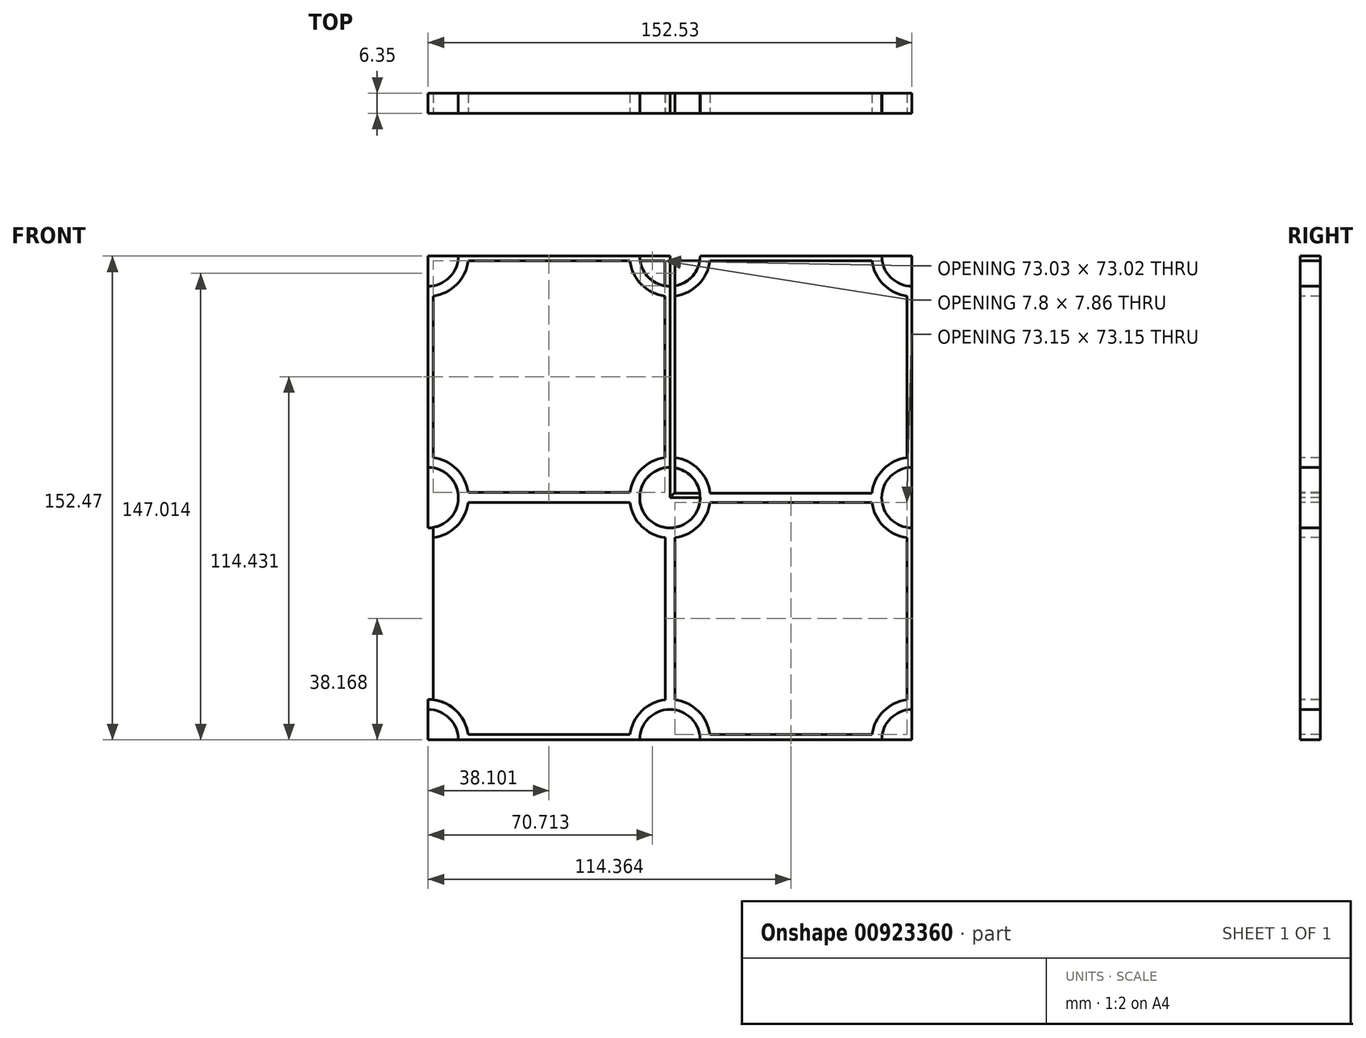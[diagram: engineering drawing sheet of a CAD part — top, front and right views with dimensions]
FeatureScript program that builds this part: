
annotation { "Feature Type Name" : "Feature", "Feature Type Description" : "" }
export const myFeature = defineFeature(function(context is Context, id is Id, definition is map)
    precondition{}
    {
        {
            var Q0;
            Q0=qCreatedBy(makeId("Front.planeOp"),FACE);
            var sketch = newSketch(context, id + "F0", { "sketchPlane" : qUnion([Q0])});
            skLineSegment(sketch, "E0.bottom", {"start": v(-162.8, 108.2) * mm, "end": v(-89.78, 108.2) * mm});
            skLineSegment(sketch, "E0.top", {"start": v(-162.8, 35.18) * mm, "end": v(-89.78, 35.18) * mm});
            skLineSegment(sketch, "E0.left", {"start": v(-162.8, 108.2) * mm, "end": v(-162.8, 35.18) * mm});
            skLineSegment(sketch, "E0.right", {"start": v(-89.78, 108.2) * mm, "end": v(-89.78, 35.18) * mm});
            skLineSegment(sketch, "E1", {"start": v(-162.8, 108.2) * mm, "end": v(-164.39, 108.2) * mm});
            skLineSegment(sketch, "E2", {"start": v(-164.39, 121.61) * mm, "end": v(-164.39, -64.06) * mm});
            skLineSegment(sketch, "E3", {"start": v(-86.6, 108.2) * mm, "end": v(-86.6, 35.26) * mm});
            skLineSegment(sketch, "E4.bottom", {"start": v(-86.6, 108.2) * mm, "end": v(-13.45, 108.2) * mm});
            skLineSegment(sketch, "E4.top", {"start": v(-86.6, 35) * mm, "end": v(-13.45, 35) * mm});
            skLineSegment(sketch, "E4.left", {"start": v(-86.6, 108.2) * mm, "end": v(-86.6, 35) * mm});
            skLineSegment(sketch, "E4.right", {"start": v(-13.45, 108.2) * mm, "end": v(-13.45, 35) * mm});
            skLineSegment(sketch, "E5.bottom", {"start": v(-162.8, 32) * mm, "end": v(-89.65, 32) * mm});
            skLineSegment(sketch, "E5.top", {"start": v(-162.8, -41.15) * mm, "end": v(-89.65, -41.15) * mm});
            skLineSegment(sketch, "E5.left", {"start": v(-162.8, 32) * mm, "end": v(-162.8, -41.15) * mm});
            skLineSegment(sketch, "E5.right", {"start": v(-89.65, 32) * mm, "end": v(-89.65, -41.15) * mm});
            skLineSegment(sketch, "E6.bottom", {"start": v(-86.6, 32) * mm, "end": v(-13.45, 32) * mm});
            skLineSegment(sketch, "E6.top", {"start": v(-86.6, -41.15) * mm, "end": v(-13.45, -41.15) * mm});
            skLineSegment(sketch, "E6.left", {"start": v(-86.6, 32) * mm, "end": v(-86.6, -41.15) * mm});
            skLineSegment(sketch, "E6.right", {"start": v(-13.45, 32) * mm, "end": v(-13.45, -41.15) * mm});
            skLineSegment(sketch, "E7", {"start": v(-86.6, 35.26) * mm, "end": v(-89.65, 32) * mm});
            skLineSegment(sketch, "E8", {"start": v(-89.78, 35.18) * mm, "end": v(-86.6, 32) * mm});
            skCircle(sketch, "E9", {"center": v(-88.18, 33.58) * mm, "radius": 9.53 * mm});
            skCircle(sketch, "E10", {"center": v(-88.18, 33.58) * mm, "radius": 12.7 * mm});
            skLineSegment(sketch, "E11.0", {"start": v(-200.1, 109.73) * mm, "end": v(15.54, 109.73) * mm});
            skPoint(sketch, "E12.orphan", {"position": v(-164.39, 0) * mm});
            skLineSegment(sketch, "E13.0", {"start": v(-212.16, -42.74) * mm, "end": v(20.66, -42.74) * mm});
            skLineSegment(sketch, "E14.0", {"start": v(-11.86, 123.44) * mm, "end": v(-11.86, -68.08) * mm});
            skLineSegment(sketch, "E15", {"start": v(-11.86, 33.58) * mm, "end": v(-190.66, 33.58) * mm});
            skLineSegment(sketch, "E16", {"start": v(-88.18, 109.73) * mm, "end": v(-88.18, -48) * mm});
            skLineSegment(sketch, "E17", {"start": v(-88.18, -48) * mm, "end": v(-87.03, -48) * mm});
            skCircle(sketch, "E18", {"center": v(-164.39, 109.73) * mm, "radius": 12.7 * mm});
            skCircle(sketch, "E19", {"center": v(-88.18, 109.73) * mm, "radius": 12.7 * mm});
            skCircle(sketch, "E20", {"center": v(-11.86, 109.73) * mm, "radius": 12.7 * mm});
            skCircle(sketch, "E21", {"center": v(-11.86, 33.58) * mm, "radius": 12.7 * mm});
            skCircle(sketch, "E22", {"center": v(-88.18, -42.74) * mm, "radius": 12.7 * mm});
            skCircle(sketch, "E23", {"center": v(-164.39, 33.58) * mm, "radius": 12.7 * mm});
            skCircle(sketch, "E24", {"center": v(-164.39, 33.58) * mm, "radius": 9.53 * mm});
            skCircle(sketch, "E25", {"center": v(-88.18, -42.74) * mm, "radius": 9.53 * mm});
            skCircle(sketch, "E26", {"center": v(-164.39, -42.74) * mm, "radius": 9.53 * mm});
            skCircle(sketch, "E27", {"center": v(-11.86, -42.74) * mm, "radius": 9.53 * mm});
            skCircle(sketch, "E28", {"center": v(-11.86, 33.58) * mm, "radius": 9.53 * mm});
            skCircle(sketch, "E29", {"center": v(-11.86, 109.73) * mm, "radius": 9.53 * mm});
            skCircle(sketch, "E30", {"center": v(-88.18, 109.73) * mm, "radius": 9.53 * mm});
            skCircle(sketch, "E31", {"center": v(-164.39, 109.73) * mm, "radius": 9.53 * mm});
            skCircle(sketch, "E32", {"center": v(-164.39, -42.74) * mm, "radius": 12.7 * mm});
            skCircle(sketch, "E33", {"center": v(-11.86, -42.74) * mm, "radius": 12.7 * mm});
            skSolve(sketch);
        }
        {
            var Q0;
            Q0=makeQuery(id+"F0.imprint","IMPRINT",FACE,{"disambiguationData":[TD([[makeQuery(id+"F0.imprint","IMPRINT",EDGE,{"derivedFrom":sQuery(id+"F0.wireOp",EDGE,"E0.bottom")}),-1.0]])]});
            extrude(context, id + "F1", {"entities" : qUnion([Q0]), "oppositeDirection" : true, "depth" : 6.35 * mm, "offsetDistance" : 30.48 * mm});
        }
        {
            var Q0;
            Q0=makeQuery(id+"F1.opExtrude","SWEPT_BODY",BODY,{"disambiguationData":[OSD([sQuery(id+"F0.wireOp",EDGE,"E0.bottom"),sQuery(id+"F0.wireOp",EDGE,"E0.left"),sQuery(id+"F0.wireOp",EDGE,"E31")])]});
            deleteBodies(context, id + "F2", {"entities" : qUnion([Q0])});
        }
        {
            var Q0;
            Q0=makeQuery(id+"F1.opExtrude","SWEPT_BODY",BODY,{"disambiguationData":[OSD([sQuery(id+"F0.wireOp",EDGE,"E0.bottom"),sQuery(id+"F0.wireOp",EDGE,"E0.right"),sQuery(id+"F0.wireOp",EDGE,"E30")])]});
            deleteBodies(context, id + "F3", {"entities" : qUnion([Q0])});
        }
        {
            var Q0;
            {var subQ7=sQuery(id+"F0.wireOp",EDGE,"E18");var subQ13=sQuery(id+"F0.wireOp",EDGE,"E0.bottom");var subQ14=makeQuery(id+"F0.imprint","INTERSECT",VERTEX,{"derivedFrom":[subQ13,subQ7]});Q0=makeQuery(id+"F0.imprint","IMPRINT",FACE,{"disambiguationData":[TD([[makeQuery(id+"F0.imprint","IMPRINT",EDGE,{"disambiguationData":[TD([[subQ14,-1.0]])],"derivedFrom":subQ13}),-1.0]])]});}
            var Q1;
            {var subQ9=sQuery(id+"F0.wireOp",EDGE,"E19");var subQ13=sQuery(id+"F0.wireOp",EDGE,"E4.bottom");var subQ14=makeQuery(id+"F0.imprint","INTERSECT",VERTEX,{"derivedFrom":[subQ13,subQ9]});Q1=makeQuery(id+"F0.imprint","IMPRINT",FACE,{"disambiguationData":[TD([[makeQuery(id+"F0.imprint","IMPRINT",EDGE,{"disambiguationData":[TD([[subQ14,-1.0]])],"derivedFrom":subQ13}),-1.0]])]});}
            var Q2;
            {var subQ10=sQuery(id+"F0.wireOp",EDGE,"E10");var subQ13=sQuery(id+"F0.wireOp",EDGE,"E6.bottom");var subQ14=makeQuery(id+"F0.imprint","INTERSECT",VERTEX,{"derivedFrom":[subQ13,subQ10]});Q2=makeQuery(id+"F0.imprint","IMPRINT",FACE,{"disambiguationData":[TD([[makeQuery(id+"F0.imprint","IMPRINT",EDGE,{"disambiguationData":[TD([[subQ14,-1.0]])],"derivedFrom":subQ13}),-1.0]])]});}
            var Q3;
            {var subQ10=sQuery(id+"F0.wireOp",EDGE,"E23");var subQ13=sQuery(id+"F0.wireOp",EDGE,"E5.bottom");var subQ14=makeQuery(id+"F0.imprint","INTERSECT",VERTEX,{"derivedFrom":[subQ13,subQ10]});Q3=makeQuery(id+"F0.imprint","IMPRINT",FACE,{"disambiguationData":[TD([[makeQuery(id+"F0.imprint","IMPRINT",EDGE,{"disambiguationData":[TD([[subQ14,-1.0]])],"derivedFrom":subQ13}),-1.0]])]});}
            extrude(context, id + "F4", {"entities" : qUnion([Q0, Q1, Q2, Q3]), "oppositeDirection" : true, "depth" : 6.35 * mm, "offsetDistance" : 30.48 * mm});
        }
        {
            var Q0;
            {var subQ0=sQuery(id+"F0.wireOp",EDGE,"E0.left");var subQ1=sQuery(id+"F0.wireOp",EDGE,"E0.top");var subQ2=makeQuery(id+"F0.imprint","INTERSECT",VERTEX,{"derivedFrom":[subQ1,subQ0]});Q0=makeQuery(id+"F0.imprint","IMPRINT",FACE,{"disambiguationData":[TD([[makeQuery(id+"F0.imprint","IMPRINT",EDGE,{"disambiguationData":[TD([[subQ2,-1.0]])],"derivedFrom":subQ1}),1.0]])]});}
            var Q1;
            {var subQ0=sQuery(id+"F0.wireOp",EDGE,"E5.left");var subQ1=sQuery(id+"F0.wireOp",EDGE,"E5.bottom");var subQ2=makeQuery(id+"F0.imprint","INTERSECT",VERTEX,{"derivedFrom":[subQ1,subQ0]});Q1=makeQuery(id+"F0.imprint","IMPRINT",FACE,{"disambiguationData":[TD([[makeQuery(id+"F0.imprint","IMPRINT",EDGE,{"disambiguationData":[TD([[subQ2,-1.0]])],"derivedFrom":subQ1}),-1.0]])]});}
            var Q2;
            {var subQ0=sQuery(id+"F0.wireOp",EDGE,"E4.left");var subQ1=sQuery(id+"F0.wireOp",EDGE,"E4.top");var subQ2=makeQuery(id+"F0.imprint","INTERSECT",VERTEX,{"derivedFrom":[subQ1,subQ0]});Q2=makeQuery(id+"F0.imprint","IMPRINT",FACE,{"disambiguationData":[TD([[makeQuery(id+"F0.imprint","IMPRINT",EDGE,{"disambiguationData":[TD([[subQ2,-1.0]])],"derivedFrom":subQ1}),1.0]])]});}
            var Q3;
            {var subQ1=sQuery(id+"F0.wireOp",EDGE,"E0.top");var subQ3=sQuery(id+"F0.wireOp",EDGE,"E9");var subQ4=makeQuery(id+"F0.imprint","INTERSECT",VERTEX,{"derivedFrom":[subQ1,subQ3]});Q3=makeQuery(id+"F0.imprint","IMPRINT",FACE,{"disambiguationData":[TD([[makeQuery(id+"F0.imprint","IMPRINT",EDGE,{"disambiguationData":[TD([[subQ4,1.0]])],"derivedFrom":subQ3}),1.0]])]});}
            var Q4;
            {var subQ1=sQuery(id+"F0.wireOp",EDGE,"E5.bottom");var subQ3=sQuery(id+"F0.wireOp",EDGE,"E9");var subQ4=makeQuery(id+"F0.imprint","INTERSECT",VERTEX,{"derivedFrom":[subQ1,subQ3]});Q4=makeQuery(id+"F0.imprint","IMPRINT",FACE,{"disambiguationData":[TD([[makeQuery(id+"F0.imprint","IMPRINT",EDGE,{"disambiguationData":[TD([[subQ4,-1.0]])],"derivedFrom":subQ3}),1.0]])]});}
            var Q5;
            {var subQ1=sQuery(id+"F0.wireOp",EDGE,"E6.bottom");var subQ3=sQuery(id+"F0.wireOp",EDGE,"E9");var subQ4=makeQuery(id+"F0.imprint","INTERSECT",VERTEX,{"derivedFrom":[subQ1,subQ3]});Q5=makeQuery(id+"F0.imprint","IMPRINT",FACE,{"disambiguationData":[TD([[makeQuery(id+"F0.imprint","IMPRINT",EDGE,{"disambiguationData":[TD([[subQ4,1.0]])],"derivedFrom":subQ3}),1.0]])]});}
            var Q6;
            {var subQ0=sQuery(id+"F0.wireOp",EDGE,"E7");var subQ1=sQuery(id+"F0.wireOp",EDGE,"E4.left");var subQ2=makeQuery(id+"F0.imprint","INTERSECT",VERTEX,{"derivedFrom":[subQ1,subQ0]});Q6=makeQuery(id+"F0.imprint","IMPRINT",FACE,{"disambiguationData":[TD([[makeQuery(id+"F0.imprint","IMPRINT",EDGE,{"disambiguationData":[TD([[subQ2,1.0]])],"derivedFrom":subQ1}),-1.0]])]});}
            var Q7;
            {var subQ1=sQuery(id+"F0.wireOp",EDGE,"E4.left");var subQ6=sQuery(id+"F0.wireOp",EDGE,"E4.top");var subQ9=makeQuery(id+"F0.imprint","INTERSECT",VERTEX,{"derivedFrom":[subQ6,subQ1]});Q7=makeQuery(id+"F0.imprint","IMPRINT",FACE,{"disambiguationData":[TD([[makeQuery(id+"F0.imprint","IMPRINT",EDGE,{"disambiguationData":[TD([[subQ9,-1.0]])],"derivedFrom":subQ6}),-1.0]])]});}
            var Q8;
            {var subQ1=sQuery(id+"F0.wireOp",EDGE,"E6.bottom");var subQ3=sQuery(id+"F0.wireOp",EDGE,"E9");var subQ4=makeQuery(id+"F0.imprint","INTERSECT",VERTEX,{"derivedFrom":[subQ1,subQ3]});Q8=makeQuery(id+"F0.imprint","IMPRINT",FACE,{"disambiguationData":[TD([[makeQuery(id+"F0.imprint","IMPRINT",EDGE,{"disambiguationData":[TD([[subQ4,-1.0]])],"derivedFrom":subQ3}),1.0]])]});}
            var Q9;
            {var subQ1=sQuery(id+"F0.wireOp",EDGE,"E6.left");var subQ3=sQuery(id+"F0.wireOp",EDGE,"E9");var subQ4=makeQuery(id+"F0.imprint","INTERSECT",VERTEX,{"derivedFrom":[subQ1,subQ3]});Q9=makeQuery(id+"F0.imprint","IMPRINT",FACE,{"disambiguationData":[TD([[makeQuery(id+"F0.imprint","IMPRINT",EDGE,{"disambiguationData":[TD([[subQ4,1.0]])],"derivedFrom":subQ3}),1.0]])]});}
            var Q10;
            {var subQ1=sQuery(id+"F0.wireOp",EDGE,"E5.right");var subQ3=sQuery(id+"F0.wireOp",EDGE,"E9");var subQ4=makeQuery(id+"F0.imprint","INTERSECT",VERTEX,{"derivedFrom":[subQ1,subQ3]});Q10=makeQuery(id+"F0.imprint","IMPRINT",FACE,{"disambiguationData":[TD([[makeQuery(id+"F0.imprint","IMPRINT",EDGE,{"disambiguationData":[TD([[subQ4,-1.0]])],"derivedFrom":subQ3}),1.0]])]});}
            var Q11;
            {var subQ1=sQuery(id+"F0.wireOp",EDGE,"E0.right");var subQ3=sQuery(id+"F0.wireOp",EDGE,"E9");var subQ4=makeQuery(id+"F0.imprint","INTERSECT",VERTEX,{"derivedFrom":[subQ1,subQ3]});Q11=makeQuery(id+"F0.imprint","IMPRINT",FACE,{"disambiguationData":[TD([[makeQuery(id+"F0.imprint","IMPRINT",EDGE,{"disambiguationData":[TD([[subQ4,1.0]])],"derivedFrom":subQ3}),1.0]])]});}
            var Q12;
            {var subQ1=sQuery(id+"F0.wireOp",EDGE,"E0.top");var subQ3=sQuery(id+"F0.wireOp",EDGE,"E9");var subQ4=makeQuery(id+"F0.imprint","INTERSECT",VERTEX,{"derivedFrom":[subQ1,subQ3]});Q12=makeQuery(id+"F0.imprint","IMPRINT",FACE,{"disambiguationData":[TD([[makeQuery(id+"F0.imprint","IMPRINT",EDGE,{"disambiguationData":[TD([[subQ4,-1.0]])],"derivedFrom":subQ3}),1.0]])]});}
            var Q13;
            {var subQ1=sQuery(id+"F0.wireOp",EDGE,"E5.bottom");var subQ3=sQuery(id+"F0.wireOp",EDGE,"E9");var subQ4=makeQuery(id+"F0.imprint","INTERSECT",VERTEX,{"derivedFrom":[subQ1,subQ3]});Q13=makeQuery(id+"F0.imprint","IMPRINT",FACE,{"disambiguationData":[TD([[makeQuery(id+"F0.imprint","IMPRINT",EDGE,{"disambiguationData":[TD([[subQ4,1.0]])],"derivedFrom":subQ3}),1.0]])]});}
            var Q14;
            {var subQ5=sQuery(id+"F0.wireOp",EDGE,"E0.left");var subQ6=sQuery(id+"F0.wireOp",EDGE,"E0.top");var subQ7=makeQuery(id+"F0.imprint","INTERSECT",VERTEX,{"derivedFrom":[subQ6,subQ5]});Q14=makeQuery(id+"F0.imprint","IMPRINT",FACE,{"disambiguationData":[TD([[makeQuery(id+"F0.imprint","IMPRINT",EDGE,{"disambiguationData":[TD([[subQ7,-1.0]])],"derivedFrom":subQ6}),-1.0]])]});}
            var Q15;
            {var subQ0=sQuery(id+"F0.wireOp",EDGE,"E15");var subQ1=sQuery(id+"F0.wireOp",EDGE,"E2");var subQ2=makeQuery(id+"F0.imprint","INTERSECT",VERTEX,{"derivedFrom":[subQ1,subQ0]});Q15=makeQuery(id+"F0.imprint","IMPRINT",FACE,{"disambiguationData":[TD([[makeQuery(id+"F0.imprint","IMPRINT",EDGE,{"disambiguationData":[TD([[subQ2,-1.0]])],"derivedFrom":subQ1}),1.0]])]});}
            var Q16;
            {var subQ0=sQuery(id+"F0.wireOp",EDGE,"E4.right");var subQ1=sQuery(id+"F0.wireOp",EDGE,"E4.top");var subQ2=makeQuery(id+"F0.imprint","INTERSECT",VERTEX,{"derivedFrom":[subQ1,subQ0]});Q16=makeQuery(id+"F0.imprint","IMPRINT",FACE,{"disambiguationData":[TD([[makeQuery(id+"F0.imprint","IMPRINT",EDGE,{"disambiguationData":[TD([[subQ2,1.0]])],"derivedFrom":subQ1}),1.0]])]});}
            var Q17;
            {var subQ6=sQuery(id+"F0.wireOp",EDGE,"E4.top");var subQ8=sQuery(id+"F0.wireOp",EDGE,"E4.right");var subQ9=makeQuery(id+"F0.imprint","INTERSECT",VERTEX,{"derivedFrom":[subQ6,subQ8]});Q17=makeQuery(id+"F0.imprint","IMPRINT",FACE,{"disambiguationData":[TD([[makeQuery(id+"F0.imprint","IMPRINT",EDGE,{"disambiguationData":[TD([[subQ9,1.0]])],"derivedFrom":subQ6}),-1.0]])]});}
            var Q18;
            {var subQ5=sQuery(id+"F0.wireOp",EDGE,"E6.bottom");var subQ8=sQuery(id+"F0.wireOp",EDGE,"E6.right");var subQ9=makeQuery(id+"F0.imprint","INTERSECT",VERTEX,{"derivedFrom":[subQ5,subQ8]});Q18=makeQuery(id+"F0.imprint","IMPRINT",FACE,{"disambiguationData":[TD([[makeQuery(id+"F0.imprint","IMPRINT",EDGE,{"disambiguationData":[TD([[subQ9,1.0]])],"derivedFrom":subQ5}),1.0]])]});}
            var Q19;
            {var subQ0=sQuery(id+"F0.wireOp",EDGE,"E6.right");var subQ1=sQuery(id+"F0.wireOp",EDGE,"E6.bottom");var subQ2=makeQuery(id+"F0.imprint","INTERSECT",VERTEX,{"derivedFrom":[subQ1,subQ0]});Q19=makeQuery(id+"F0.imprint","IMPRINT",FACE,{"disambiguationData":[TD([[makeQuery(id+"F0.imprint","IMPRINT",EDGE,{"disambiguationData":[TD([[subQ2,1.0]])],"derivedFrom":subQ1}),-1.0]])]});}
            var Q20;
            {var subQ0=sQuery(id+"F0.wireOp",EDGE,"E4.right");var subQ1=sQuery(id+"F0.wireOp",EDGE,"E4.bottom");var subQ2=makeQuery(id+"F0.imprint","INTERSECT",VERTEX,{"derivedFrom":[subQ1,subQ0]});Q20=makeQuery(id+"F0.imprint","IMPRINT",FACE,{"disambiguationData":[TD([[makeQuery(id+"F0.imprint","IMPRINT",EDGE,{"disambiguationData":[TD([[subQ2,1.0]])],"derivedFrom":subQ1}),-1.0]])]});}
            var Q21;
            {var subQ5=sQuery(id+"F0.wireOp",EDGE,"E4.right");var subQ6=sQuery(id+"F0.wireOp",EDGE,"E4.bottom");var subQ7=makeQuery(id+"F0.imprint","INTERSECT",VERTEX,{"derivedFrom":[subQ6,subQ5]});Q21=makeQuery(id+"F0.imprint","IMPRINT",FACE,{"disambiguationData":[TD([[makeQuery(id+"F0.imprint","IMPRINT",EDGE,{"disambiguationData":[TD([[subQ7,1.0]])],"derivedFrom":subQ6}),1.0]])]});}
            var Q22;
            {var subQ0=sQuery(id+"F0.wireOp",EDGE,"E4.left");var subQ1=sQuery(id+"F0.wireOp",EDGE,"E4.bottom");var subQ2=makeQuery(id+"F0.imprint","INTERSECT",VERTEX,{"derivedFrom":[subQ1,subQ0]});Q22=makeQuery(id+"F0.imprint","IMPRINT",FACE,{"disambiguationData":[TD([[makeQuery(id+"F0.imprint","IMPRINT",EDGE,{"disambiguationData":[TD([[subQ2,-1.0]])],"derivedFrom":subQ1}),-1.0]])]});}
            var Q23;
            {var subQ0=sQuery(id+"F0.wireOp",EDGE,"E0.right");var subQ1=sQuery(id+"F0.wireOp",EDGE,"E0.bottom");var subQ2=makeQuery(id+"F0.imprint","INTERSECT",VERTEX,{"derivedFrom":[subQ1,subQ0]});Q23=makeQuery(id+"F0.imprint","IMPRINT",FACE,{"disambiguationData":[TD([[makeQuery(id+"F0.imprint","IMPRINT",EDGE,{"disambiguationData":[TD([[subQ2,1.0]])],"derivedFrom":subQ1}),-1.0]])]});}
            var Q24;
            {var subQ6=sQuery(id+"F0.wireOp",EDGE,"E0.right");var subQ7=sQuery(id+"F0.wireOp",EDGE,"E0.bottom");var subQ8=makeQuery(id+"F0.imprint","INTERSECT",VERTEX,{"derivedFrom":[subQ7,subQ6]});Q24=makeQuery(id+"F0.imprint","IMPRINT",FACE,{"disambiguationData":[TD([[makeQuery(id+"F0.imprint","IMPRINT",EDGE,{"disambiguationData":[TD([[subQ8,1.0]])],"derivedFrom":subQ7}),1.0]])]});}
            var Q25;
            {var subQ5=sQuery(id+"F0.wireOp",EDGE,"E4.left");var subQ6=sQuery(id+"F0.wireOp",EDGE,"E4.bottom");var subQ7=makeQuery(id+"F0.imprint","INTERSECT",VERTEX,{"derivedFrom":[subQ6,subQ5]});Q25=makeQuery(id+"F0.imprint","IMPRINT",FACE,{"disambiguationData":[TD([[makeQuery(id+"F0.imprint","IMPRINT",EDGE,{"disambiguationData":[TD([[subQ7,-1.0]])],"derivedFrom":subQ6}),1.0]])]});}
            var Q26;
            {var subQ1=sQuery(id+"F0.wireOp",EDGE,"E0.bottom");var subQ3=sQuery(id+"F0.wireOp",EDGE,"E31");var subQ4=makeQuery(id+"F0.imprint","INTERSECT",VERTEX,{"derivedFrom":[subQ1,subQ3]});Q26=makeQuery(id+"F0.imprint","IMPRINT",FACE,{"disambiguationData":[TD([[makeQuery(id+"F0.imprint","IMPRINT",EDGE,{"disambiguationData":[TD([[subQ4,1.0]])],"derivedFrom":subQ3}),1.0]])]});}
            var Q27;
            {var subQ0=sQuery(id+"F0.wireOp",EDGE,"E1");Q27=makeQuery(id+"F0.imprint","IMPRINT",FACE,{"disambiguationData":[TD([[makeQuery(id+"F0.imprint","IMPRINT",EDGE,{"derivedFrom":subQ0}),1.0]])]});}
            var Q28;
            {var subQ7=sQuery(id+"F0.wireOp",EDGE,"E1");Q28=makeQuery(id+"F0.imprint","IMPRINT",FACE,{"disambiguationData":[TD([[makeQuery(id+"F0.imprint","IMPRINT",EDGE,{"derivedFrom":subQ7}),-1.0]])]});}
            var Q29;
            {var subQ0=sQuery(id+"F0.wireOp",EDGE,"E6.right");var subQ1=sQuery(id+"F0.wireOp",EDGE,"E6.top");var subQ2=makeQuery(id+"F0.imprint","INTERSECT",VERTEX,{"derivedFrom":[subQ1,subQ0]});Q29=makeQuery(id+"F0.imprint","IMPRINT",FACE,{"disambiguationData":[TD([[makeQuery(id+"F0.imprint","IMPRINT",EDGE,{"disambiguationData":[TD([[subQ2,1.0]])],"derivedFrom":subQ1}),1.0]])]});}
            var Q30;
            {var subQ0=sQuery(id+"F0.wireOp",EDGE,"E6.left");var subQ1=sQuery(id+"F0.wireOp",EDGE,"E6.top");var subQ2=makeQuery(id+"F0.imprint","INTERSECT",VERTEX,{"derivedFrom":[subQ1,subQ0]});Q30=makeQuery(id+"F0.imprint","IMPRINT",FACE,{"disambiguationData":[TD([[makeQuery(id+"F0.imprint","IMPRINT",EDGE,{"disambiguationData":[TD([[subQ2,-1.0]])],"derivedFrom":subQ1}),1.0]])]});}
            var Q31;
            {var subQ0=sQuery(id+"F0.wireOp",EDGE,"E5.right");var subQ1=sQuery(id+"F0.wireOp",EDGE,"E5.top");var subQ2=makeQuery(id+"F0.imprint","INTERSECT",VERTEX,{"derivedFrom":[subQ1,subQ0]});Q31=makeQuery(id+"F0.imprint","IMPRINT",FACE,{"disambiguationData":[TD([[makeQuery(id+"F0.imprint","IMPRINT",EDGE,{"disambiguationData":[TD([[subQ2,1.0]])],"derivedFrom":subQ1}),1.0]])]});}
            var Q32;
            {var subQ6=sQuery(id+"F0.wireOp",EDGE,"E6.right");var subQ7=sQuery(id+"F0.wireOp",EDGE,"E6.top");var subQ8=makeQuery(id+"F0.imprint","INTERSECT",VERTEX,{"derivedFrom":[subQ7,subQ6]});Q32=makeQuery(id+"F0.imprint","IMPRINT",FACE,{"disambiguationData":[TD([[makeQuery(id+"F0.imprint","IMPRINT",EDGE,{"disambiguationData":[TD([[subQ8,1.0]])],"derivedFrom":subQ7}),-1.0]])]});}
            var Q33;
            {var subQ6=sQuery(id+"F0.wireOp",EDGE,"E6.left");var subQ7=sQuery(id+"F0.wireOp",EDGE,"E6.top");var subQ8=makeQuery(id+"F0.imprint","INTERSECT",VERTEX,{"derivedFrom":[subQ7,subQ6]});Q33=makeQuery(id+"F0.imprint","IMPRINT",FACE,{"disambiguationData":[TD([[makeQuery(id+"F0.imprint","IMPRINT",EDGE,{"disambiguationData":[TD([[subQ8,-1.0]])],"derivedFrom":subQ7}),-1.0]])]});}
            var Q34;
            {var subQ6=sQuery(id+"F0.wireOp",EDGE,"E5.right");var subQ7=sQuery(id+"F0.wireOp",EDGE,"E5.top");var subQ8=makeQuery(id+"F0.imprint","INTERSECT",VERTEX,{"derivedFrom":[subQ7,subQ6]});Q34=makeQuery(id+"F0.imprint","IMPRINT",FACE,{"disambiguationData":[TD([[makeQuery(id+"F0.imprint","IMPRINT",EDGE,{"disambiguationData":[TD([[subQ8,1.0]])],"derivedFrom":subQ7}),-1.0]])]});}
            var Q35;
            {var subQ0=sQuery(id+"F0.wireOp",EDGE,"E5.left");var subQ1=sQuery(id+"F0.wireOp",EDGE,"E5.top");var subQ2=makeQuery(id+"F0.imprint","INTERSECT",VERTEX,{"derivedFrom":[subQ1,subQ0]});Q35=makeQuery(id+"F0.imprint","IMPRINT",FACE,{"disambiguationData":[TD([[makeQuery(id+"F0.imprint","IMPRINT",EDGE,{"disambiguationData":[TD([[subQ2,-1.0]])],"derivedFrom":subQ1}),1.0]])]});}
            var Q36;
            {var subQ1=sQuery(id+"F0.wireOp",EDGE,"E2");var subQ3=sQuery(id+"F0.wireOp",EDGE,"E26");var subQ10=makeQuery(id+"F0.imprint","INTERSECT",VERTEX,{"disambiguationData":[OD(0.0)],"derivedFrom":[subQ1,subQ3]});Q36=makeQuery(id+"F0.imprint","IMPRINT",FACE,{"disambiguationData":[TD([[makeQuery(id+"F0.imprint","IMPRINT",EDGE,{"disambiguationData":[TD([[subQ10,-1.0]])],"derivedFrom":subQ1}),1.0]])]});}
            extrude(context, id + "F5", {"entities" : qUnion([Q0, Q1, Q2, Q3, Q4, Q5, Q6, Q7, Q8, Q9, Q10, Q11, Q12, Q13, Q14, Q15, Q16, Q17, Q18, Q19, Q20, Q21, Q22, Q23, Q24, Q25, Q26, Q27, Q28, Q29, Q30, Q31, Q32, Q33, Q34, Q35, Q36]), "oppositeDirection" : true, "depth" : 6.35 * mm, "offsetDistance" : 30.48 * mm});
        }
        {
            var Q0;
            Q0=makeQuery(id+"F5.opExtrude","CAP_FACE",FACE,{"disambiguationData":[OSD([sQuery(id+"F0.wireOp",EDGE,"E11.0"),sQuery(id+"F0.wireOp",EDGE,"E14.0"),sQuery(id+"F0.wireOp",EDGE,"E29")])],"isStart":true});
            extrude(context, id + "F6", {"entities" : qUnion([Q0]), "operationType" : NewBodyOperationType.ADD, "oppositeDirection" : true, "depth" : 6.35 * mm, "offsetDistance" : 30.48 * mm});
        }
        {
            var Q0;
            {var subQ0=sQuery(id+"F0.wireOp",EDGE,"E31");var subQ1=sQuery(id+"F0.wireOp",EDGE,"E0.bottom");var subQ2=makeQuery(id+"F0.imprint","INTERSECT",VERTEX,{"derivedFrom":[subQ1,subQ0]});Q0=makeQuery(id+"F0.imprint","IMPRINT",FACE,{"disambiguationData":[TD([[makeQuery(id+"F0.imprint","IMPRINT",EDGE,{"disambiguationData":[TD([[subQ2,-1.0]])],"derivedFrom":subQ1}),-1.0]])]});}
            var Q1;
            {var subQ0=sQuery(id+"F0.wireOp",EDGE,"E18");var subQ1=sQuery(id+"F0.wireOp",EDGE,"E0.bottom");var subQ2=makeQuery(id+"F0.imprint","INTERSECT",VERTEX,{"derivedFrom":[subQ1,subQ0]});Q1=makeQuery(id+"F0.imprint","IMPRINT",FACE,{"disambiguationData":[TD([[makeQuery(id+"F0.imprint","IMPRINT",EDGE,{"disambiguationData":[TD([[subQ2,-1.0]])],"derivedFrom":subQ1}),1.0]])]});}
            var Q2;
            {var subQ0=sQuery(id+"F0.wireOp",EDGE,"E19");var subQ1=sQuery(id+"F0.wireOp",EDGE,"E0.bottom");var subQ2=makeQuery(id+"F0.imprint","INTERSECT",VERTEX,{"derivedFrom":[subQ1,subQ0]});Q2=makeQuery(id+"F0.imprint","IMPRINT",FACE,{"disambiguationData":[TD([[makeQuery(id+"F0.imprint","IMPRINT",EDGE,{"disambiguationData":[TD([[subQ2,-1.0]])],"derivedFrom":subQ1}),-1.0]])]});}
            var Q3;
            {var subQ0=sQuery(id+"F0.wireOp",EDGE,"E19");var subQ1=sQuery(id+"F0.wireOp",EDGE,"E0.bottom");var subQ2=makeQuery(id+"F0.imprint","INTERSECT",VERTEX,{"derivedFrom":[subQ1,subQ0]});Q3=makeQuery(id+"F0.imprint","IMPRINT",FACE,{"disambiguationData":[TD([[makeQuery(id+"F0.imprint","IMPRINT",EDGE,{"disambiguationData":[TD([[subQ2,-1.0]])],"derivedFrom":subQ1}),1.0]])]});}
            var Q4;
            {var subQ0=sQuery(id+"F0.wireOp",EDGE,"E30");var subQ1=sQuery(id+"F0.wireOp",EDGE,"E0.right");var subQ2=makeQuery(id+"F0.imprint","INTERSECT",VERTEX,{"derivedFrom":[subQ1,subQ0]});Q4=makeQuery(id+"F0.imprint","IMPRINT",FACE,{"disambiguationData":[TD([[makeQuery(id+"F0.imprint","IMPRINT",EDGE,{"disambiguationData":[TD([[subQ2,-1.0]])],"derivedFrom":subQ1}),1.0]])]});}
            var Q5;
            {var subQ0=sQuery(id+"F0.wireOp",EDGE,"E30");var subQ1=sQuery(id+"F0.wireOp",EDGE,"E4.left");var subQ2=makeQuery(id+"F0.imprint","INTERSECT",VERTEX,{"derivedFrom":[subQ1,subQ0]});Q5=makeQuery(id+"F0.imprint","IMPRINT",FACE,{"disambiguationData":[TD([[makeQuery(id+"F0.imprint","IMPRINT",EDGE,{"disambiguationData":[TD([[subQ2,-1.0]])],"derivedFrom":subQ1}),-1.0]])]});}
            var Q6;
            {var subQ5=sQuery(id+"F0.wireOp",EDGE,"E4.left");var subQ6=sQuery(id+"F0.wireOp",EDGE,"E4.bottom");var subQ7=makeQuery(id+"F0.imprint","INTERSECT",VERTEX,{"derivedFrom":[subQ6,subQ5]});Q6=makeQuery(id+"F0.imprint","IMPRINT",FACE,{"disambiguationData":[TD([[makeQuery(id+"F0.imprint","IMPRINT",EDGE,{"disambiguationData":[TD([[subQ7,-1.0]])],"derivedFrom":subQ6}),1.0]])]});}
            var Q7;
            {var subQ6=sQuery(id+"F0.wireOp",EDGE,"E0.right");var subQ7=sQuery(id+"F0.wireOp",EDGE,"E0.bottom");var subQ8=makeQuery(id+"F0.imprint","INTERSECT",VERTEX,{"derivedFrom":[subQ7,subQ6]});Q7=makeQuery(id+"F0.imprint","IMPRINT",FACE,{"disambiguationData":[TD([[makeQuery(id+"F0.imprint","IMPRINT",EDGE,{"disambiguationData":[TD([[subQ8,1.0]])],"derivedFrom":subQ7}),1.0]])]});}
            var Q8;
            {var subQ0=sQuery(id+"F0.wireOp",EDGE,"E30");var subQ1=sQuery(id+"F0.wireOp",EDGE,"E4.bottom");var subQ2=makeQuery(id+"F0.imprint","INTERSECT",VERTEX,{"derivedFrom":[subQ1,subQ0]});Q8=makeQuery(id+"F0.imprint","IMPRINT",FACE,{"disambiguationData":[TD([[makeQuery(id+"F0.imprint","IMPRINT",EDGE,{"disambiguationData":[TD([[subQ2,-1.0]])],"derivedFrom":subQ1}),-1.0]])]});}
            var Q9;
            {var subQ0=sQuery(id+"F0.wireOp",EDGE,"E31");var subQ1=sQuery(id+"F0.wireOp",EDGE,"E0.bottom");var subQ2=makeQuery(id+"F0.imprint","INTERSECT",VERTEX,{"derivedFrom":[subQ1,subQ0]});Q9=makeQuery(id+"F0.imprint","IMPRINT",FACE,{"disambiguationData":[TD([[makeQuery(id+"F0.imprint","IMPRINT",EDGE,{"disambiguationData":[TD([[subQ2,-1.0]])],"derivedFrom":subQ1}),1.0]])]});}
            var Q10;
            {var subQ0=sQuery(id+"F0.wireOp",EDGE,"E31");var subQ1=sQuery(id+"F0.wireOp",EDGE,"E0.left");var subQ2=makeQuery(id+"F0.imprint","INTERSECT",VERTEX,{"derivedFrom":[subQ1,subQ0]});Q10=makeQuery(id+"F0.imprint","IMPRINT",FACE,{"disambiguationData":[TD([[makeQuery(id+"F0.imprint","IMPRINT",EDGE,{"disambiguationData":[TD([[subQ2,-1.0]])],"derivedFrom":subQ1}),-1.0]])]});}
            var Q11;
            {var subQ0=sQuery(id+"F0.wireOp",EDGE,"E18");var subQ1=sQuery(id+"F0.wireOp",EDGE,"E0.left");var subQ2=makeQuery(id+"F0.imprint","INTERSECT",VERTEX,{"derivedFrom":[subQ1,subQ0]});Q11=makeQuery(id+"F0.imprint","IMPRINT",FACE,{"disambiguationData":[TD([[makeQuery(id+"F0.imprint","IMPRINT",EDGE,{"disambiguationData":[TD([[subQ2,-1.0]])],"derivedFrom":subQ1}),-1.0]])]});}
            var Q12;
            {var subQ0=sQuery(id+"F0.wireOp",EDGE,"E19");var subQ1=sQuery(id+"F0.wireOp",EDGE,"E4.left");var subQ2=makeQuery(id+"F0.imprint","INTERSECT",VERTEX,{"derivedFrom":[subQ1,subQ0]});Q12=makeQuery(id+"F0.imprint","IMPRINT",FACE,{"disambiguationData":[TD([[makeQuery(id+"F0.imprint","IMPRINT",EDGE,{"disambiguationData":[TD([[subQ2,-1.0]])],"derivedFrom":subQ1}),-1.0]])]});}
            var Q13;
            {var subQ0=sQuery(id+"F0.wireOp",EDGE,"E19");var subQ1=sQuery(id+"F0.wireOp",EDGE,"E0.right");var subQ2=makeQuery(id+"F0.imprint","INTERSECT",VERTEX,{"derivedFrom":[subQ1,subQ0]});Q13=makeQuery(id+"F0.imprint","IMPRINT",FACE,{"disambiguationData":[TD([[makeQuery(id+"F0.imprint","IMPRINT",EDGE,{"disambiguationData":[TD([[subQ2,-1.0]])],"derivedFrom":subQ1}),1.0]])]});}
            var Q14;
            {var subQ0=sQuery(id+"F0.wireOp",EDGE,"E9");var subQ1=sQuery(id+"F0.wireOp",EDGE,"E4.top");var subQ2=makeQuery(id+"F0.imprint","INTERSECT",VERTEX,{"derivedFrom":[subQ1,subQ0]});Q14=makeQuery(id+"F0.imprint","IMPRINT",FACE,{"disambiguationData":[TD([[makeQuery(id+"F0.imprint","IMPRINT",EDGE,{"disambiguationData":[TD([[subQ2,-1.0]])],"derivedFrom":subQ1}),1.0]])]});}
            var Q15;
            {var subQ0=sQuery(id+"F0.wireOp",EDGE,"E10");var subQ1=sQuery(id+"F0.wireOp",EDGE,"E0.top");var subQ2=makeQuery(id+"F0.imprint","INTERSECT",VERTEX,{"derivedFrom":[subQ1,subQ0]});Q15=makeQuery(id+"F0.imprint","IMPRINT",FACE,{"disambiguationData":[TD([[makeQuery(id+"F0.imprint","IMPRINT",EDGE,{"disambiguationData":[TD([[subQ2,-1.0]])],"derivedFrom":subQ1}),1.0]])]});}
            var Q16;
            {var subQ0=sQuery(id+"F0.wireOp",EDGE,"E10");var subQ1=sQuery(id+"F0.wireOp",EDGE,"E4.left");var subQ2=makeQuery(id+"F0.imprint","INTERSECT",VERTEX,{"derivedFrom":[subQ1,subQ0]});Q16=makeQuery(id+"F0.imprint","IMPRINT",FACE,{"disambiguationData":[TD([[makeQuery(id+"F0.imprint","IMPRINT",EDGE,{"disambiguationData":[TD([[subQ2,-1.0]])],"derivedFrom":subQ1}),-1.0]])]});}
            var Q17;
            {var subQ0=sQuery(id+"F0.wireOp",EDGE,"E10");var subQ1=sQuery(id+"F0.wireOp",EDGE,"E0.right");var subQ2=makeQuery(id+"F0.imprint","INTERSECT",VERTEX,{"derivedFrom":[subQ1,subQ0]});Q17=makeQuery(id+"F0.imprint","IMPRINT",FACE,{"disambiguationData":[TD([[makeQuery(id+"F0.imprint","IMPRINT",EDGE,{"disambiguationData":[TD([[subQ2,-1.0]])],"derivedFrom":subQ1}),1.0]])]});}
            var Q18;
            {var subQ0=sQuery(id+"F0.wireOp",EDGE,"E19");var subQ1=sQuery(id+"F0.wireOp",EDGE,"E4.bottom");var subQ2=makeQuery(id+"F0.imprint","INTERSECT",VERTEX,{"derivedFrom":[subQ1,subQ0]});Q18=makeQuery(id+"F0.imprint","IMPRINT",FACE,{"disambiguationData":[TD([[makeQuery(id+"F0.imprint","IMPRINT",EDGE,{"disambiguationData":[TD([[subQ2,-1.0]])],"derivedFrom":subQ1}),1.0]])]});}
            var Q19;
            {var subQ0=sQuery(id+"F0.wireOp",EDGE,"E30");var subQ1=sQuery(id+"F0.wireOp",EDGE,"E4.bottom");var subQ2=makeQuery(id+"F0.imprint","INTERSECT",VERTEX,{"derivedFrom":[subQ1,subQ0]});Q19=makeQuery(id+"F0.imprint","IMPRINT",FACE,{"disambiguationData":[TD([[makeQuery(id+"F0.imprint","IMPRINT",EDGE,{"disambiguationData":[TD([[subQ2,-1.0]])],"derivedFrom":subQ1}),1.0]])]});}
            var Q20;
            {var subQ0=sQuery(id+"F0.wireOp",EDGE,"E20");var subQ1=sQuery(id+"F0.wireOp",EDGE,"E4.bottom");var subQ2=makeQuery(id+"F0.imprint","INTERSECT",VERTEX,{"derivedFrom":[subQ1,subQ0]});Q20=makeQuery(id+"F0.imprint","IMPRINT",FACE,{"disambiguationData":[TD([[makeQuery(id+"F0.imprint","IMPRINT",EDGE,{"disambiguationData":[TD([[subQ2,-1.0]])],"derivedFrom":subQ1}),-1.0]])]});}
            var Q21;
            {var subQ0=sQuery(id+"F0.wireOp",EDGE,"E20");var subQ1=sQuery(id+"F0.wireOp",EDGE,"E4.bottom");var subQ2=makeQuery(id+"F0.imprint","INTERSECT",VERTEX,{"derivedFrom":[subQ1,subQ0]});Q21=makeQuery(id+"F0.imprint","IMPRINT",FACE,{"disambiguationData":[TD([[makeQuery(id+"F0.imprint","IMPRINT",EDGE,{"disambiguationData":[TD([[subQ2,-1.0]])],"derivedFrom":subQ1}),1.0]])]});}
            var Q22;
            {var subQ0=sQuery(id+"F0.wireOp",EDGE,"E29");var subQ1=sQuery(id+"F0.wireOp",EDGE,"E4.right");var subQ2=makeQuery(id+"F0.imprint","INTERSECT",VERTEX,{"derivedFrom":[subQ1,subQ0]});Q22=makeQuery(id+"F0.imprint","IMPRINT",FACE,{"disambiguationData":[TD([[makeQuery(id+"F0.imprint","IMPRINT",EDGE,{"disambiguationData":[TD([[subQ2,-1.0]])],"derivedFrom":subQ1}),1.0]])]});}
            var Q23;
            {var subQ0=sQuery(id+"F0.wireOp",EDGE,"E20");var subQ1=sQuery(id+"F0.wireOp",EDGE,"E4.right");var subQ2=makeQuery(id+"F0.imprint","INTERSECT",VERTEX,{"derivedFrom":[subQ1,subQ0]});Q23=makeQuery(id+"F0.imprint","IMPRINT",FACE,{"disambiguationData":[TD([[makeQuery(id+"F0.imprint","IMPRINT",EDGE,{"disambiguationData":[TD([[subQ2,-1.0]])],"derivedFrom":subQ1}),1.0]])]});}
            var Q24;
            {var subQ0=sQuery(id+"F0.wireOp",EDGE,"E21");var subQ1=sQuery(id+"F0.wireOp",EDGE,"E4.top");var subQ2=makeQuery(id+"F0.imprint","INTERSECT",VERTEX,{"derivedFrom":[subQ1,subQ0]});Q24=makeQuery(id+"F0.imprint","IMPRINT",FACE,{"disambiguationData":[TD([[makeQuery(id+"F0.imprint","IMPRINT",EDGE,{"disambiguationData":[TD([[subQ2,-1.0]])],"derivedFrom":subQ1}),1.0]])]});}
            var Q25;
            {var subQ0=sQuery(id+"F0.wireOp",EDGE,"E21");var subQ1=sQuery(id+"F0.wireOp",EDGE,"E4.right");var subQ2=makeQuery(id+"F0.imprint","INTERSECT",VERTEX,{"derivedFrom":[subQ1,subQ0]});Q25=makeQuery(id+"F0.imprint","IMPRINT",FACE,{"disambiguationData":[TD([[makeQuery(id+"F0.imprint","IMPRINT",EDGE,{"disambiguationData":[TD([[subQ2,-1.0]])],"derivedFrom":subQ1}),1.0]])]});}
            var Q26;
            {var subQ0=sQuery(id+"F0.wireOp",EDGE,"E21");var subQ1=sQuery(id+"F0.wireOp",EDGE,"E6.bottom");var subQ2=makeQuery(id+"F0.imprint","INTERSECT",VERTEX,{"derivedFrom":[subQ1,subQ0]});Q26=makeQuery(id+"F0.imprint","IMPRINT",FACE,{"disambiguationData":[TD([[makeQuery(id+"F0.imprint","IMPRINT",EDGE,{"disambiguationData":[TD([[subQ2,-1.0]])],"derivedFrom":subQ1}),1.0]])]});}
            var Q27;
            {var subQ0=sQuery(id+"F0.wireOp",EDGE,"E21");var subQ1=sQuery(id+"F0.wireOp",EDGE,"E4.top");var subQ2=makeQuery(id+"F0.imprint","INTERSECT",VERTEX,{"derivedFrom":[subQ1,subQ0]});Q27=makeQuery(id+"F0.imprint","IMPRINT",FACE,{"disambiguationData":[TD([[makeQuery(id+"F0.imprint","IMPRINT",EDGE,{"disambiguationData":[TD([[subQ2,-1.0]])],"derivedFrom":subQ1}),-1.0]])]});}
            var Q28;
            {var subQ0=sQuery(id+"F0.wireOp",EDGE,"E10");var subQ1=sQuery(id+"F0.wireOp",EDGE,"E6.bottom");var subQ2=makeQuery(id+"F0.imprint","INTERSECT",VERTEX,{"derivedFrom":[subQ1,subQ0]});Q28=makeQuery(id+"F0.imprint","IMPRINT",FACE,{"disambiguationData":[TD([[makeQuery(id+"F0.imprint","IMPRINT",EDGE,{"disambiguationData":[TD([[subQ2,-1.0]])],"derivedFrom":subQ1}),1.0]])]});}
            var Q29;
            {var subQ0=sQuery(id+"F0.wireOp",EDGE,"E10");var subQ1=sQuery(id+"F0.wireOp",EDGE,"E4.top");var subQ2=makeQuery(id+"F0.imprint","INTERSECT",VERTEX,{"derivedFrom":[subQ1,subQ0]});Q29=makeQuery(id+"F0.imprint","IMPRINT",FACE,{"disambiguationData":[TD([[makeQuery(id+"F0.imprint","IMPRINT",EDGE,{"disambiguationData":[TD([[subQ2,-1.0]])],"derivedFrom":subQ1}),-1.0]])]});}
            var Q30;
            {var subQ0=sQuery(id+"F0.wireOp",EDGE,"E21");var subQ1=sQuery(id+"F0.wireOp",EDGE,"E6.bottom");var subQ2=makeQuery(id+"F0.imprint","INTERSECT",VERTEX,{"derivedFrom":[subQ1,subQ0]});Q30=makeQuery(id+"F0.imprint","IMPRINT",FACE,{"disambiguationData":[TD([[makeQuery(id+"F0.imprint","IMPRINT",EDGE,{"disambiguationData":[TD([[subQ2,-1.0]])],"derivedFrom":subQ1}),-1.0]])]});}
            var Q31;
            {var subQ0=sQuery(id+"F0.wireOp",EDGE,"E21");var subQ1=sQuery(id+"F0.wireOp",EDGE,"E6.right");var subQ2=makeQuery(id+"F0.imprint","INTERSECT",VERTEX,{"derivedFrom":[subQ1,subQ0]});Q31=makeQuery(id+"F0.imprint","IMPRINT",FACE,{"disambiguationData":[TD([[makeQuery(id+"F0.imprint","IMPRINT",EDGE,{"disambiguationData":[TD([[subQ2,-1.0]])],"derivedFrom":subQ1}),1.0]])]});}
            var Q32;
            {var subQ0=sQuery(id+"F0.wireOp",EDGE,"E28");var subQ1=sQuery(id+"F0.wireOp",EDGE,"E6.right");var subQ2=makeQuery(id+"F0.imprint","INTERSECT",VERTEX,{"derivedFrom":[subQ1,subQ0]});Q32=makeQuery(id+"F0.imprint","IMPRINT",FACE,{"disambiguationData":[TD([[makeQuery(id+"F0.imprint","IMPRINT",EDGE,{"disambiguationData":[TD([[subQ2,-1.0]])],"derivedFrom":subQ1}),1.0]])]});}
            var Q33;
            {var subQ0=sQuery(id+"F0.wireOp",EDGE,"E10");var subQ1=sQuery(id+"F0.wireOp",EDGE,"E0.top");var subQ2=makeQuery(id+"F0.imprint","INTERSECT",VERTEX,{"derivedFrom":[subQ1,subQ0]});Q33=makeQuery(id+"F0.imprint","IMPRINT",FACE,{"disambiguationData":[TD([[makeQuery(id+"F0.imprint","IMPRINT",EDGE,{"disambiguationData":[TD([[subQ2,-1.0]])],"derivedFrom":subQ1}),-1.0]])]});}
            var Q34;
            {var subQ0=sQuery(id+"F0.wireOp",EDGE,"E10");var subQ1=sQuery(id+"F0.wireOp",EDGE,"E5.bottom");var subQ2=makeQuery(id+"F0.imprint","INTERSECT",VERTEX,{"derivedFrom":[subQ1,subQ0]});Q34=makeQuery(id+"F0.imprint","IMPRINT",FACE,{"disambiguationData":[TD([[makeQuery(id+"F0.imprint","IMPRINT",EDGE,{"disambiguationData":[TD([[subQ2,-1.0]])],"derivedFrom":subQ1}),1.0]])]});}
            var Q35;
            {var subQ0=sQuery(id+"F0.wireOp",EDGE,"E9");var subQ1=sQuery(id+"F0.wireOp",EDGE,"E4.top");var subQ2=makeQuery(id+"F0.imprint","INTERSECT",VERTEX,{"derivedFrom":[subQ1,subQ0]});Q35=makeQuery(id+"F0.imprint","IMPRINT",FACE,{"disambiguationData":[TD([[makeQuery(id+"F0.imprint","IMPRINT",EDGE,{"disambiguationData":[TD([[subQ2,-1.0]])],"derivedFrom":subQ1}),-1.0]])]});}
            var Q36;
            {var subQ0=sQuery(id+"F0.wireOp",EDGE,"E9");var subQ1=sQuery(id+"F0.wireOp",EDGE,"E6.bottom");var subQ2=makeQuery(id+"F0.imprint","INTERSECT",VERTEX,{"derivedFrom":[subQ1,subQ0]});Q36=makeQuery(id+"F0.imprint","IMPRINT",FACE,{"disambiguationData":[TD([[makeQuery(id+"F0.imprint","IMPRINT",EDGE,{"disambiguationData":[TD([[subQ2,-1.0]])],"derivedFrom":subQ1}),1.0]])]});}
            var Q37;
            {var subQ0=sQuery(id+"F0.wireOp",EDGE,"E9");var subQ1=sQuery(id+"F0.wireOp",EDGE,"E6.bottom");var subQ2=makeQuery(id+"F0.imprint","INTERSECT",VERTEX,{"derivedFrom":[subQ1,subQ0]});Q37=makeQuery(id+"F0.imprint","IMPRINT",FACE,{"disambiguationData":[TD([[makeQuery(id+"F0.imprint","IMPRINT",EDGE,{"disambiguationData":[TD([[subQ2,-1.0]])],"derivedFrom":subQ1}),-1.0]])]});}
            var Q38;
            {var subQ0=sQuery(id+"F0.wireOp",EDGE,"E9");var subQ1=sQuery(id+"F0.wireOp",EDGE,"E6.left");var subQ2=makeQuery(id+"F0.imprint","INTERSECT",VERTEX,{"derivedFrom":[subQ1,subQ0]});Q38=makeQuery(id+"F0.imprint","IMPRINT",FACE,{"disambiguationData":[TD([[makeQuery(id+"F0.imprint","IMPRINT",EDGE,{"disambiguationData":[TD([[subQ2,-1.0]])],"derivedFrom":subQ1}),-1.0]])]});}
            var Q39;
            {var subQ0=sQuery(id+"F0.wireOp",EDGE,"E9");var subQ1=sQuery(id+"F0.wireOp",EDGE,"E5.right");var subQ2=makeQuery(id+"F0.imprint","INTERSECT",VERTEX,{"derivedFrom":[subQ1,subQ0]});Q39=makeQuery(id+"F0.imprint","IMPRINT",FACE,{"disambiguationData":[TD([[makeQuery(id+"F0.imprint","IMPRINT",EDGE,{"disambiguationData":[TD([[subQ2,-1.0]])],"derivedFrom":subQ1}),1.0]])]});}
            var Q40;
            {var subQ0=sQuery(id+"F0.wireOp",EDGE,"E10");var subQ1=sQuery(id+"F0.wireOp",EDGE,"E5.bottom");var subQ2=makeQuery(id+"F0.imprint","INTERSECT",VERTEX,{"derivedFrom":[subQ1,subQ0]});Q40=makeQuery(id+"F0.imprint","IMPRINT",FACE,{"disambiguationData":[TD([[makeQuery(id+"F0.imprint","IMPRINT",EDGE,{"disambiguationData":[TD([[subQ2,-1.0]])],"derivedFrom":subQ1}),-1.0]])]});}
            var Q41;
            {var subQ0=sQuery(id+"F0.wireOp",EDGE,"E23");var subQ1=sQuery(id+"F0.wireOp",EDGE,"E0.top");var subQ2=makeQuery(id+"F0.imprint","INTERSECT",VERTEX,{"derivedFrom":[subQ1,subQ0]});Q41=makeQuery(id+"F0.imprint","IMPRINT",FACE,{"disambiguationData":[TD([[makeQuery(id+"F0.imprint","IMPRINT",EDGE,{"disambiguationData":[TD([[subQ2,-1.0]])],"derivedFrom":subQ1}),-1.0]])]});}
            var Q42;
            {var subQ0=sQuery(id+"F0.wireOp",EDGE,"E23");var subQ1=sQuery(id+"F0.wireOp",EDGE,"E5.bottom");var subQ2=makeQuery(id+"F0.imprint","INTERSECT",VERTEX,{"derivedFrom":[subQ1,subQ0]});Q42=makeQuery(id+"F0.imprint","IMPRINT",FACE,{"disambiguationData":[TD([[makeQuery(id+"F0.imprint","IMPRINT",EDGE,{"disambiguationData":[TD([[subQ2,-1.0]])],"derivedFrom":subQ1}),1.0]])]});}
            var Q43;
            {var subQ0=sQuery(id+"F0.wireOp",EDGE,"E24");var subQ1=sQuery(id+"F0.wireOp",EDGE,"E0.top");var subQ2=makeQuery(id+"F0.imprint","INTERSECT",VERTEX,{"derivedFrom":[subQ1,subQ0]});Q43=makeQuery(id+"F0.imprint","IMPRINT",FACE,{"disambiguationData":[TD([[makeQuery(id+"F0.imprint","IMPRINT",EDGE,{"disambiguationData":[TD([[subQ2,-1.0]])],"derivedFrom":subQ1}),-1.0]])]});}
            var Q44;
            {var subQ0=sQuery(id+"F0.wireOp",EDGE,"E24");var subQ1=sQuery(id+"F0.wireOp",EDGE,"E5.bottom");var subQ2=makeQuery(id+"F0.imprint","INTERSECT",VERTEX,{"derivedFrom":[subQ1,subQ0]});Q44=makeQuery(id+"F0.imprint","IMPRINT",FACE,{"disambiguationData":[TD([[makeQuery(id+"F0.imprint","IMPRINT",EDGE,{"disambiguationData":[TD([[subQ2,-1.0]])],"derivedFrom":subQ1}),1.0]])]});}
            var Q45;
            {var subQ0=sQuery(id+"F0.wireOp",EDGE,"E24");var subQ1=sQuery(id+"F0.wireOp",EDGE,"E0.top");var subQ2=makeQuery(id+"F0.imprint","INTERSECT",VERTEX,{"derivedFrom":[subQ1,subQ0]});Q45=makeQuery(id+"F0.imprint","IMPRINT",FACE,{"disambiguationData":[TD([[makeQuery(id+"F0.imprint","IMPRINT",EDGE,{"disambiguationData":[TD([[subQ2,-1.0]])],"derivedFrom":subQ1}),1.0]])]});}
            var Q46;
            {var subQ0=sQuery(id+"F0.wireOp",EDGE,"E24");var subQ1=sQuery(id+"F0.wireOp",EDGE,"E5.bottom");var subQ2=makeQuery(id+"F0.imprint","INTERSECT",VERTEX,{"derivedFrom":[subQ1,subQ0]});Q46=makeQuery(id+"F0.imprint","IMPRINT",FACE,{"disambiguationData":[TD([[makeQuery(id+"F0.imprint","IMPRINT",EDGE,{"disambiguationData":[TD([[subQ2,-1.0]])],"derivedFrom":subQ1}),-1.0]])]});}
            var Q47;
            {var subQ0=sQuery(id+"F0.wireOp",EDGE,"E23");var subQ1=sQuery(id+"F0.wireOp",EDGE,"E2");var subQ2=makeQuery(id+"F0.imprint","INTERSECT",VERTEX,{"disambiguationData":[OD(1.0)],"derivedFrom":[subQ1,subQ0]});Q47=makeQuery(id+"F0.imprint","IMPRINT",FACE,{"disambiguationData":[TD([[makeQuery(id+"F0.imprint","IMPRINT",EDGE,{"disambiguationData":[TD([[subQ2,1.0]])],"derivedFrom":subQ1}),1.0]])]});}
            var Q48;
            {var subQ0=sQuery(id+"F0.wireOp",EDGE,"E23");var subQ1=sQuery(id+"F0.wireOp",EDGE,"E0.left");var subQ2=makeQuery(id+"F0.imprint","INTERSECT",VERTEX,{"derivedFrom":[subQ1,subQ0]});Q48=makeQuery(id+"F0.imprint","IMPRINT",FACE,{"disambiguationData":[TD([[makeQuery(id+"F0.imprint","IMPRINT",EDGE,{"disambiguationData":[TD([[subQ2,-1.0]])],"derivedFrom":subQ1}),-1.0]])]});}
            var Q49;
            {var subQ0=sQuery(id+"F0.wireOp",EDGE,"E10");var subQ1=sQuery(id+"F0.wireOp",EDGE,"E6.left");var subQ2=makeQuery(id+"F0.imprint","INTERSECT",VERTEX,{"derivedFrom":[subQ1,subQ0]});Q49=makeQuery(id+"F0.imprint","IMPRINT",FACE,{"disambiguationData":[TD([[makeQuery(id+"F0.imprint","IMPRINT",EDGE,{"disambiguationData":[TD([[subQ2,-1.0]])],"derivedFrom":subQ1}),-1.0]])]});}
            var Q50;
            {var subQ0=sQuery(id+"F0.wireOp",EDGE,"E10");var subQ1=sQuery(id+"F0.wireOp",EDGE,"E5.right");var subQ2=makeQuery(id+"F0.imprint","INTERSECT",VERTEX,{"derivedFrom":[subQ1,subQ0]});Q50=makeQuery(id+"F0.imprint","IMPRINT",FACE,{"disambiguationData":[TD([[makeQuery(id+"F0.imprint","IMPRINT",EDGE,{"disambiguationData":[TD([[subQ2,-1.0]])],"derivedFrom":subQ1}),1.0]])]});}
            var Q51;
            {var subQ0=sQuery(id+"F0.wireOp",EDGE,"E23");var subQ1=sQuery(id+"F0.wireOp",EDGE,"E2");var subQ2=makeQuery(id+"F0.imprint","INTERSECT",VERTEX,{"disambiguationData":[OD(1.0)],"derivedFrom":[subQ1,subQ0]});Q51=makeQuery(id+"F0.imprint","IMPRINT",FACE,{"disambiguationData":[TD([[makeQuery(id+"F0.imprint","IMPRINT",EDGE,{"disambiguationData":[TD([[subQ2,-1.0]])],"derivedFrom":subQ1}),1.0]])]});}
            var Q52;
            {var subQ0=sQuery(id+"F0.wireOp",EDGE,"E26");var subQ1=sQuery(id+"F0.wireOp",EDGE,"E5.top");var subQ2=makeQuery(id+"F0.imprint","INTERSECT",VERTEX,{"derivedFrom":[subQ1,subQ0]});Q52=makeQuery(id+"F0.imprint","IMPRINT",FACE,{"disambiguationData":[TD([[makeQuery(id+"F0.imprint","IMPRINT",EDGE,{"disambiguationData":[TD([[subQ2,-1.0]])],"derivedFrom":subQ1}),1.0]])]});}
            var Q53;
            {var subQ0=sQuery(id+"F0.wireOp",EDGE,"E32");var subQ1=sQuery(id+"F0.wireOp",EDGE,"E2");var subQ2=makeQuery(id+"F0.imprint","INTERSECT",VERTEX,{"disambiguationData":[OD(1.0)],"derivedFrom":[subQ1,subQ0]});Q53=makeQuery(id+"F0.imprint","IMPRINT",FACE,{"disambiguationData":[TD([[makeQuery(id+"F0.imprint","IMPRINT",EDGE,{"disambiguationData":[TD([[subQ2,-1.0]])],"derivedFrom":subQ1}),1.0]])]});}
            var Q54;
            {var subQ0=sQuery(id+"F0.wireOp",EDGE,"E26");var subQ1=sQuery(id+"F0.wireOp",EDGE,"E5.top");var subQ2=makeQuery(id+"F0.imprint","INTERSECT",VERTEX,{"derivedFrom":[subQ1,subQ0]});Q54=makeQuery(id+"F0.imprint","IMPRINT",FACE,{"disambiguationData":[TD([[makeQuery(id+"F0.imprint","IMPRINT",EDGE,{"disambiguationData":[TD([[subQ2,-1.0]])],"derivedFrom":subQ1}),-1.0]])]});}
            var Q55;
            {var subQ0=sQuery(id+"F0.wireOp",EDGE,"E32");var subQ1=sQuery(id+"F0.wireOp",EDGE,"E5.top");var subQ2=makeQuery(id+"F0.imprint","INTERSECT",VERTEX,{"derivedFrom":[subQ1,subQ0]});Q55=makeQuery(id+"F0.imprint","IMPRINT",FACE,{"disambiguationData":[TD([[makeQuery(id+"F0.imprint","IMPRINT",EDGE,{"disambiguationData":[TD([[subQ2,-1.0]])],"derivedFrom":subQ1}),-1.0]])]});}
            var Q56;
            {var subQ0=sQuery(id+"F0.wireOp",EDGE,"E22");var subQ1=sQuery(id+"F0.wireOp",EDGE,"E5.top");var subQ2=makeQuery(id+"F0.imprint","INTERSECT",VERTEX,{"derivedFrom":[subQ1,subQ0]});Q56=makeQuery(id+"F0.imprint","IMPRINT",FACE,{"disambiguationData":[TD([[makeQuery(id+"F0.imprint","IMPRINT",EDGE,{"disambiguationData":[TD([[subQ2,-1.0]])],"derivedFrom":subQ1}),1.0]])]});}
            var Q57;
            {var subQ0=sQuery(id+"F0.wireOp",EDGE,"E22");var subQ1=sQuery(id+"F0.wireOp",EDGE,"E5.top");var subQ2=makeQuery(id+"F0.imprint","INTERSECT",VERTEX,{"derivedFrom":[subQ1,subQ0]});Q57=makeQuery(id+"F0.imprint","IMPRINT",FACE,{"disambiguationData":[TD([[makeQuery(id+"F0.imprint","IMPRINT",EDGE,{"disambiguationData":[TD([[subQ2,-1.0]])],"derivedFrom":subQ1}),-1.0]])]});}
            var Q58;
            {var subQ0=sQuery(id+"F0.wireOp",EDGE,"E22");var subQ1=sQuery(id+"F0.wireOp",EDGE,"E6.left");var subQ2=makeQuery(id+"F0.imprint","INTERSECT",VERTEX,{"derivedFrom":[subQ1,subQ0]});Q58=makeQuery(id+"F0.imprint","IMPRINT",FACE,{"disambiguationData":[TD([[makeQuery(id+"F0.imprint","IMPRINT",EDGE,{"disambiguationData":[TD([[subQ2,-1.0]])],"derivedFrom":subQ1}),-1.0]])]});}
            var Q59;
            {var subQ0=sQuery(id+"F0.wireOp",EDGE,"E22");var subQ1=sQuery(id+"F0.wireOp",EDGE,"E5.right");var subQ2=makeQuery(id+"F0.imprint","INTERSECT",VERTEX,{"derivedFrom":[subQ1,subQ0]});Q59=makeQuery(id+"F0.imprint","IMPRINT",FACE,{"disambiguationData":[TD([[makeQuery(id+"F0.imprint","IMPRINT",EDGE,{"disambiguationData":[TD([[subQ2,-1.0]])],"derivedFrom":subQ1}),1.0]])]});}
            var Q60;
            {var subQ0=sQuery(id+"F0.wireOp",EDGE,"E25");var subQ1=sQuery(id+"F0.wireOp",EDGE,"E6.top");var subQ2=makeQuery(id+"F0.imprint","INTERSECT",VERTEX,{"derivedFrom":[subQ1,subQ0]});Q60=makeQuery(id+"F0.imprint","IMPRINT",FACE,{"disambiguationData":[TD([[makeQuery(id+"F0.imprint","IMPRINT",EDGE,{"disambiguationData":[TD([[subQ2,-1.0]])],"derivedFrom":subQ1}),1.0]])]});}
            var Q61;
            {var subQ0=sQuery(id+"F0.wireOp",EDGE,"E25");var subQ1=sQuery(id+"F0.wireOp",EDGE,"E6.top");var subQ2=makeQuery(id+"F0.imprint","INTERSECT",VERTEX,{"derivedFrom":[subQ1,subQ0]});Q61=makeQuery(id+"F0.imprint","IMPRINT",FACE,{"disambiguationData":[TD([[makeQuery(id+"F0.imprint","IMPRINT",EDGE,{"disambiguationData":[TD([[subQ2,-1.0]])],"derivedFrom":subQ1}),-1.0]])]});}
            var Q62;
            {var subQ0=sQuery(id+"F0.wireOp",EDGE,"E22");var subQ1=sQuery(id+"F0.wireOp",EDGE,"E6.top");var subQ2=makeQuery(id+"F0.imprint","INTERSECT",VERTEX,{"derivedFrom":[subQ1,subQ0]});Q62=makeQuery(id+"F0.imprint","IMPRINT",FACE,{"disambiguationData":[TD([[makeQuery(id+"F0.imprint","IMPRINT",EDGE,{"disambiguationData":[TD([[subQ2,-1.0]])],"derivedFrom":subQ1}),-1.0]])]});}
            var Q63;
            {var subQ0=sQuery(id+"F0.wireOp",EDGE,"E33");var subQ1=sQuery(id+"F0.wireOp",EDGE,"E6.top");var subQ2=makeQuery(id+"F0.imprint","INTERSECT",VERTEX,{"derivedFrom":[subQ1,subQ0]});Q63=makeQuery(id+"F0.imprint","IMPRINT",FACE,{"disambiguationData":[TD([[makeQuery(id+"F0.imprint","IMPRINT",EDGE,{"disambiguationData":[TD([[subQ2,-1.0]])],"derivedFrom":subQ1}),-1.0]])]});}
            var Q64;
            {var subQ0=sQuery(id+"F0.wireOp",EDGE,"E33");var subQ1=sQuery(id+"F0.wireOp",EDGE,"E6.top");var subQ2=makeQuery(id+"F0.imprint","INTERSECT",VERTEX,{"derivedFrom":[subQ1,subQ0]});Q64=makeQuery(id+"F0.imprint","IMPRINT",FACE,{"disambiguationData":[TD([[makeQuery(id+"F0.imprint","IMPRINT",EDGE,{"disambiguationData":[TD([[subQ2,-1.0]])],"derivedFrom":subQ1}),1.0]])]});}
            var Q65;
            {var subQ0=sQuery(id+"F0.wireOp",EDGE,"E33");var subQ1=sQuery(id+"F0.wireOp",EDGE,"E6.right");var subQ2=makeQuery(id+"F0.imprint","INTERSECT",VERTEX,{"derivedFrom":[subQ1,subQ0]});Q65=makeQuery(id+"F0.imprint","IMPRINT",FACE,{"disambiguationData":[TD([[makeQuery(id+"F0.imprint","IMPRINT",EDGE,{"disambiguationData":[TD([[subQ2,-1.0]])],"derivedFrom":subQ1}),1.0]])]});}
            extrude(context, id + "F7", {"entities" : qUnion([Q0, Q1, Q2, Q3, Q4, Q5, Q6, Q7, Q8, Q9, Q10, Q11, Q12, Q13, Q14, Q15, Q16, Q17, Q18, Q19, Q20, Q21, Q22, Q23, Q24, Q25, Q26, Q27, Q28, Q29, Q30, Q31, Q32, Q33, Q34, Q35, Q36, Q37, Q38, Q39, Q40, Q41, Q42, Q43, Q44, Q45, Q46, Q47, Q48, Q49, Q50, Q51, Q52, Q53, Q54, Q55, Q56, Q57, Q58, Q59, Q60, Q61, Q62, Q63, Q64, Q65]), "oppositeDirection" : true, "depth" : 6.35 * mm, "offsetDistance" : 30.48 * mm});
        }
    });
